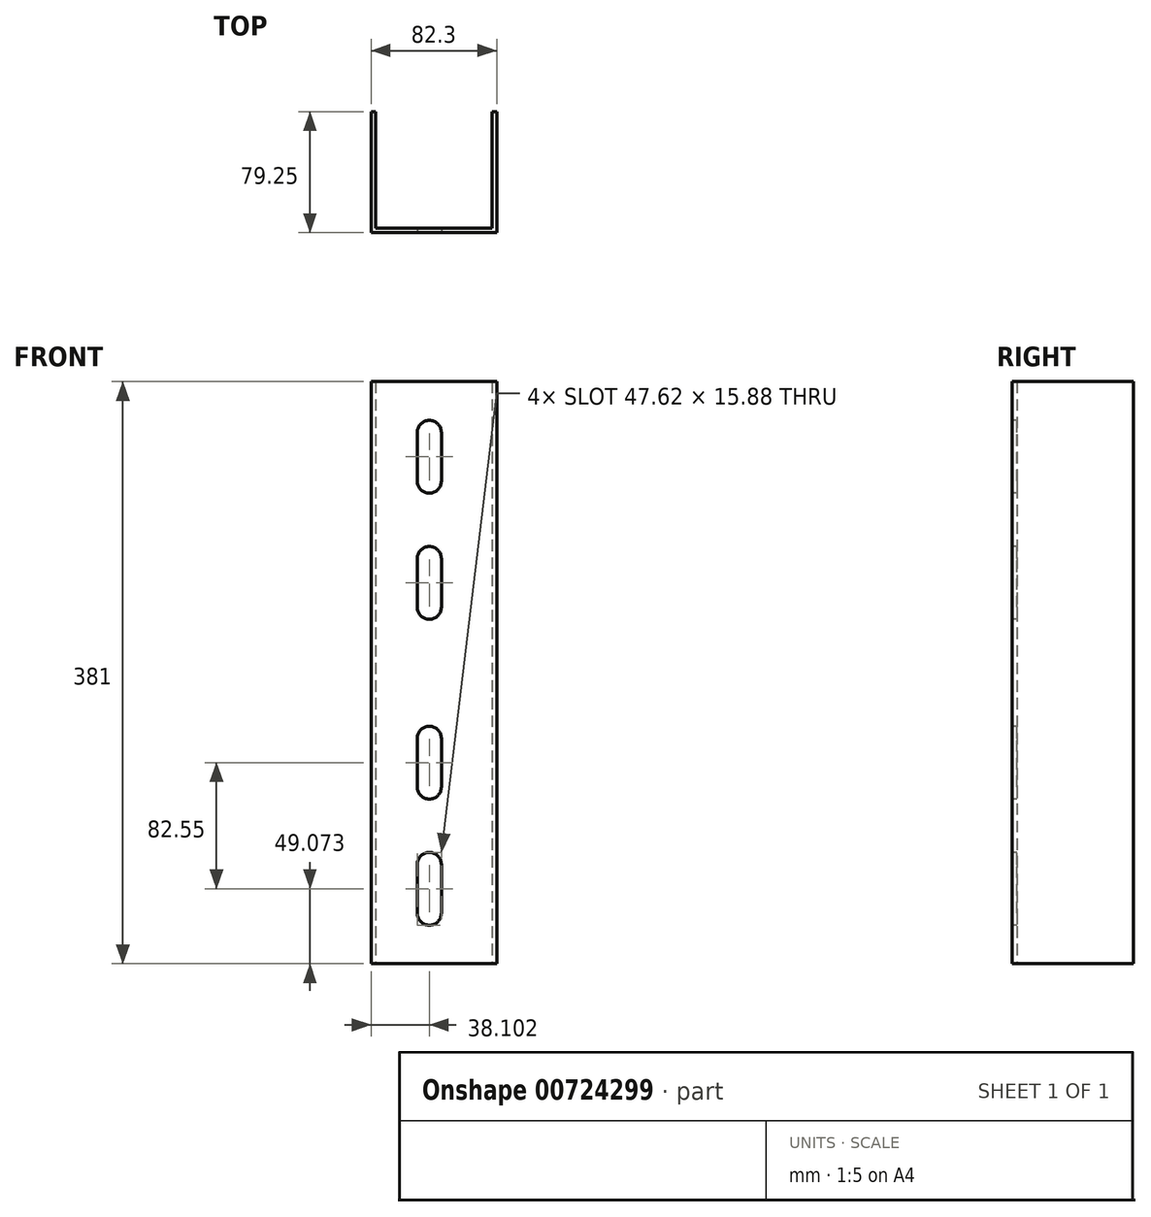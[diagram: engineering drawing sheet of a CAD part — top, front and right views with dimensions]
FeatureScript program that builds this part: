
annotation { "Feature Type Name" : "Feature", "Feature Type Description" : "" }
export const myFeature = defineFeature(function(context is Context, id is Id, definition is map)
    precondition{}
    {
        {
            var Q0;
            Q0=qCreatedBy(makeId("Top.planeOp"),FACE);
            var sketch = newSketch(context, id + "F0", { "sketchPlane" : qUnion([Q0])});
            skLineSegment(sketch, "E0.bottom", {"start": v(-41.15, -41.15) * mm, "end": v(41.15, -41.15) * mm});
            skLineSegment(sketch, "E0.top", {"start": v(-41.15, 41.15) * mm, "end": v(41.15, 41.15) * mm});
            skLineSegment(sketch, "E0.left", {"start": v(-41.15, -41.15) * mm, "end": v(-41.15, 41.15) * mm});
            skLineSegment(sketch, "E0.right", {"start": v(41.15, -41.15) * mm, "end": v(41.15, 41.15) * mm});
            skPoint(sketch, "E0.middle", {"position": v(0, 0) * mm});
            skLineSegment(sketch, "E1.bottom", {"start": v(-38.1, -38.1) * mm, "end": v(38.1, -38.1) * mm});
            skLineSegment(sketch, "E1.top", {"start": v(-38.1, 38.1) * mm, "end": v(38.1, 38.1) * mm});
            skLineSegment(sketch, "E1.left", {"start": v(-38.1, -38.1) * mm, "end": v(-38.1, 38.1) * mm});
            skLineSegment(sketch, "E1.right", {"start": v(38.1, -38.1) * mm, "end": v(38.1, 38.1) * mm});
            skLineSegment(sketch, "E2", {"start": v(-41.15, 38.07) * mm, "end": v(41.15, 38.1) * mm});
            skSolve(sketch);
        }
        {
            var Q0;
            {var subQ2=sQuery(id+"F0.wireOp",EDGE,"E0.bottom");Q0=makeQuery(id+"F0.imprint","IMPRINT",FACE,{"disambiguationData":[TD([[makeQuery(id+"F0.imprint","IMPRINT",EDGE,{"derivedFrom":subQ2}),1.0]])]});}
            extrude(context, id + "F1", {"entities" : qUnion([Q0]), "depth" : 381 * mm, "offsetDistance" : 25.4 * mm});
        }
        {
            var Q0;
            Q0=qCreatedBy(makeId("Front.planeOp"),FACE);
            cPlane(context, id + "F2", {"entities" : qUnion([Q0]), "cplaneType" : CPlaneType.OFFSET, "offset" : 50.8 * mm, "width" : 152.4 * mm, "height" : 152.4 * mm});
        }
        {
            var Q0;
            Q0=qCreatedBy(id+"F2.planeOp",FACE);
            var sketch = newSketch(context, id + "F3", { "sketchPlane" : qUnion([Q0])});
            skLineSegment(sketch, "E3", {"start": v(-10.99, 64.95) * mm, "end": v(-10.99, 33.2) * mm});
            skLineSegment(sketch, "E4", {"start": v(4.89, 64.95) * mm, "end": v(4.89, 33.2) * mm});
            skArc(sketch, "E5", {"start": v(-10.99, 64.95) * mm, "mid": v(-3.05, 72.89) * mm, "end": v(4.89, 64.95) * mm});
            skArc(sketch, "E6", {"start": v(-10.99, 33.2) * mm, "mid": v(-3.05, 25.26) * mm, "end": v(4.89, 33.2) * mm});
            skLineSegment(sketch, "E7", {"start": v(-10.99, 147.5) * mm, "end": v(-10.99, 115.75) * mm});
            skLineSegment(sketch, "E8", {"start": v(4.89, 147.5) * mm, "end": v(4.89, 115.75) * mm});
            skArc(sketch, "E9", {"start": v(-10.99, 147.5) * mm, "mid": v(-3.05, 155.44) * mm, "end": v(4.89, 147.5) * mm});
            skArc(sketch, "E10", {"start": v(-10.99, 115.75) * mm, "mid": v(-3.05, 107.81) * mm, "end": v(4.89, 115.75) * mm});
            skLineSegment(sketch, "E11", {"start": v(-10.99, 265.11) * mm, "end": v(-10.99, 233.36) * mm});
            skLineSegment(sketch, "E12", {"start": v(4.89, 265.11) * mm, "end": v(4.89, 233.36) * mm});
            skArc(sketch, "E13", {"start": v(-10.99, 265.11) * mm, "mid": v(-3.05, 273.05) * mm, "end": v(4.89, 265.11) * mm});
            skArc(sketch, "E14", {"start": v(-10.99, 233.36) * mm, "mid": v(-3.05, 225.43) * mm, "end": v(4.89, 233.36) * mm});
            skLineSegment(sketch, "E15", {"start": v(-10.99, 347.66) * mm, "end": v(-10.99, 315.91) * mm});
            skLineSegment(sketch, "E16", {"start": v(4.89, 347.66) * mm, "end": v(4.89, 315.91) * mm});
            skArc(sketch, "E17", {"start": v(-10.99, 347.66) * mm, "mid": v(-3.05, 355.6) * mm, "end": v(4.89, 347.66) * mm});
            skArc(sketch, "E18", {"start": v(-10.99, 315.91) * mm, "mid": v(-3.05, 307.98) * mm, "end": v(4.89, 315.91) * mm});
            skSolve(sketch);
        }
        {
            var Q0;
            Q0=makeQuery(id+"F3.imprint","IMPRINT",FACE,{"disambiguationData":[TD([[makeQuery(id+"F3.imprint","IMPRINT",EDGE,{"derivedFrom":sQuery(id+"F3.wireOp",EDGE,"E7")}),1.0]])]});
            var Q1;
            Q1=makeQuery(id+"F3.imprint","IMPRINT",FACE,{"disambiguationData":[TD([[makeQuery(id+"F3.imprint","IMPRINT",EDGE,{"derivedFrom":sQuery(id+"F3.wireOp",EDGE,"E3")}),1.0]])]});
            var Q2;
            Q2=makeQuery(id+"F3.imprint","IMPRINT",FACE,{"disambiguationData":[TD([[makeQuery(id+"F3.imprint","IMPRINT",EDGE,{"derivedFrom":sQuery(id+"F3.wireOp",EDGE,"E11")}),1.0]])]});
            var Q3;
            Q3=makeQuery(id+"F3.imprint","IMPRINT",FACE,{"disambiguationData":[TD([[makeQuery(id+"F3.imprint","IMPRINT",EDGE,{"derivedFrom":sQuery(id+"F3.wireOp",EDGE,"E15")}),1.0]])]});
            extrude(context, id + "F4", {"entities" : qUnion([Q0, Q1, Q2, Q3]), "operationType" : NewBodyOperationType.REMOVE, "oppositeDirection" : true, "depth" : 25.4 * mm, "offsetDistance" : 25.4 * mm});
        }
    });
